# Revit family: fx 3 pile pilecap
name_source: partatom
category: Structural Foundations
revit_build: Autodesk Revit Structure 2012 (Build: 20110309_2315)
units: mm (PartAtom-declared; Revit-internal decimal feet)

## types (3) — shared parameters
Pilcap = <By Category>
k = 3

## per-type parameters (varying)
| type | Assembly Code | Center to Bottom Spacing | Center to Top Spacing | Description | Keynote | Length | Pile Cap Depth | Pile Depth | Pile Diameter | Pile Radius | Pile Spacing | Piles | Width | r+150 |
| 3 pile pilecap 2 500 dia |  | 390 mm | 779 mm |  | 3 PILE PILECAP | 525 mm | 1200 mm | 3000 mm  [stored 9.84252 ft] | 450 mm  [stored 1.47638 ft] | 225 mm  [stored 0.738189 ft] | 1350 mm  [stored 4.42913 ft] | <By Category> | 2100 mm | 375 mm  [stored 1.23031 ft] |
| 3 pile pilecap | A1010130 | 303 mm | 606 mm |  | 3 PILE PILE CAP | 475 mm  [stored 1.5584 ft] | 1000 mm  [stored 3.28084 ft] | 5000 mm  [stored 16.4042 ft] | 350 mm  [stored 1.14829 ft] | 175 mm  [stored 0.574147 ft] | 1050 mm | Concrete - Cast-in-Place Concrete | 1700 mm  [stored 5.57743 ft] | 325 mm  [stored 1.06627 ft] |
| P3 |  | 520 mm | 1039 mm | 3 PILE PILECAP | 3 PILE PILECAP | 600 mm | 1400 mm  [stored 4.59318 ft] | 21500 mm | 600 mm | 300 mm | 1800 mm  [stored 5.90551 ft] | <By Category> | 2700 mm  [stored 8.85827 ft] | 450 mm  [stored 1.47638 ft] |

note: [stored X ft] marks values corroborated as IEEE doubles in the binary element streams (Revit-internal decimal feet)

## geometry (parser evidence)
native form markers: Sweep x2
no freeform markers — native parametric forms only
